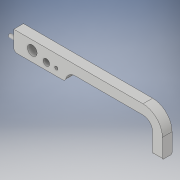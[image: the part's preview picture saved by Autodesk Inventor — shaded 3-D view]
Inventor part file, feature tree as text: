
AUTODESK INVENTOR PART (.ipt)
format: ipt  version: 2019.4 (Build 234330000, 330)  size: 147,456 bytes
history: native  units: mm
features: fillet x4, extrude x3, sketch x3, other x1
ambient origin geometry x8: Origin, YZ Plane, XZ Plane, XY Plane, X Axis, Y Axis, Z Axis, Center Point
bodies: Body1 (feature_tree)
feature tree (11):
  other  "Sólido1"
  extrude  "Extrusión1"  Depth=6000.0mm
  fillet  "Empalme1"  Radius=20000.0mm
  extrude  "Extrusión2"  Depth=3000.0mm
  fillet  "Empalme2"  Radius=1500.0mm
  fillet  "Empalme3"  Radius=500.0mm
  fillet  "Empalme4"  Radius=500.0mm
  extrude  "Extrusión3"  Depth=1500.0mm
  sketch  "Boceto1"  dims[d4=3000.0mm d5=6000.0mm d7=20000.0mm]
  sketch  "Boceto2"  dims[d8=8000.0mm d10=3000.0mm d11=1500.0mm d12=0.0mm d13=500.0mm d14=500.0mm]
  sketch  "Boceto3"  dims[d15=1000.0mm d16=1500.0mm d17=1500.0mm d18=0.0mm d19=500.0mm d20=200.0mm d21=200.0mm d24=500.0mm d26=500.0mm d27=900.0mm d28=0.0mm]
